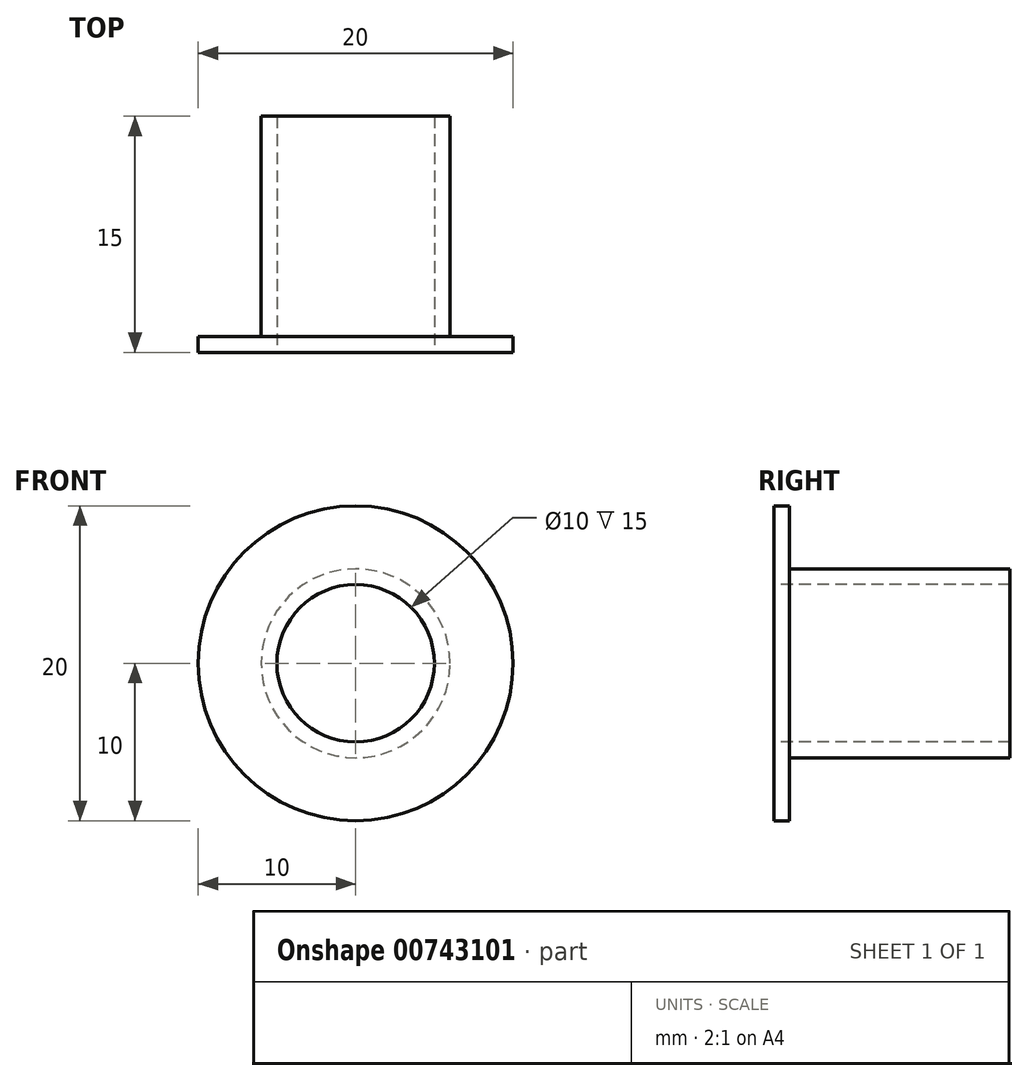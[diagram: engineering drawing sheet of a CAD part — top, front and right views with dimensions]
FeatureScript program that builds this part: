
annotation { "Feature Type Name" : "Feature", "Feature Type Description" : "" }
export const myFeature = defineFeature(function(context is Context, id is Id, definition is map)
    precondition{}
    {
        {
            var Q0;
            Q0=qCreatedBy(makeId("Front.planeOp"),FACE);
            var sketch = newSketch(context, id + "F0", { "sketchPlane" : qUnion([Q0])});
            skCircle(sketch, "E0", {"center": v(0, 0) * mm, "radius": 6 * mm});
            skCircle(sketch, "E1", {"center": v(0, 0) * mm, "radius": 5 * mm});
            skSolve(sketch);
        }
        {
            var Q0;
            Q0=qSketchRegion(id+"F0",true);
            extrude(context, id + "F1", {"entities" : qUnion([Q0]), "oppositeDirection" : true, "depth" : 15 * mm, "offsetDistance" : 25 * mm});
        }
        {
            var Q0;
            Q0=qCreatedBy(makeId("Front.planeOp"),FACE);
            var sketch = newSketch(context, id + "F2", { "sketchPlane" : qUnion([Q0])});
            skCircle(sketch, "E2.0", {"center": v(0, 0) * mm, "radius": 5 * mm});
            skCircle(sketch, "E3", {"center": v(0, 0) * mm, "radius": 10 * mm});
            skSolve(sketch);
        }
        {
            var Q0;
            Q0=qSketchRegion(id+"F2",true);
            extrude(context, id + "F3", {"entities" : qUnion([Q0]), "operationType" : NewBodyOperationType.ADD, "oppositeDirection" : true, "depth" : 1 * mm, "offsetDistance" : 25 * mm});
        }
    });
